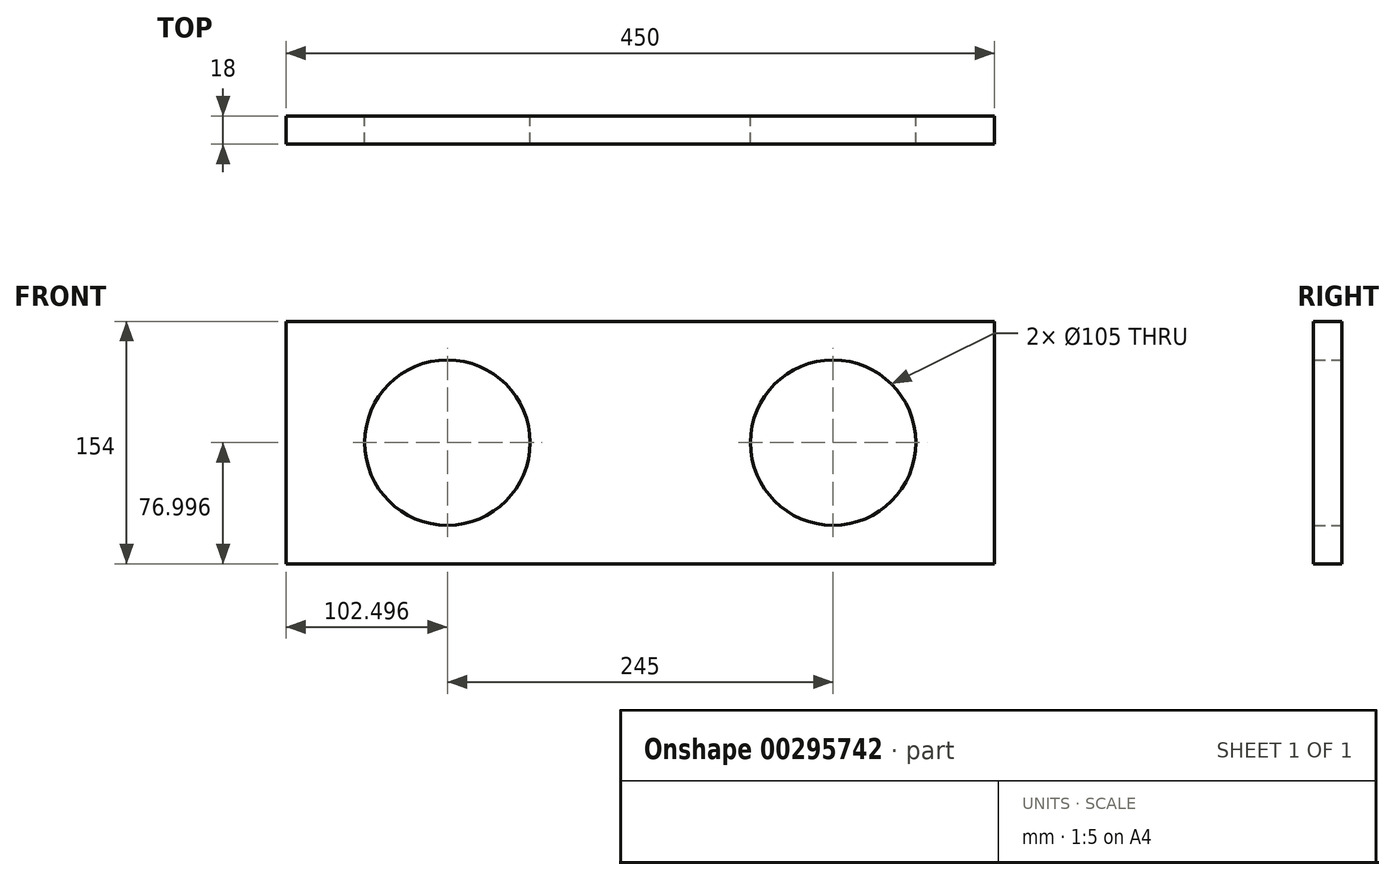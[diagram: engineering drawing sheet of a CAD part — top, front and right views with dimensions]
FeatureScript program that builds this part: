
annotation { "Feature Type Name" : "Feature", "Feature Type Description" : "" }
export const myFeature = defineFeature(function(context is Context, id is Id, definition is map)
    precondition{}
    {
        {
            var Q0;
            Q0=qCreatedBy(makeId("Front.planeOp"),FACE);
            var sketch = newSketch(context, id + "F0", { "sketchPlane" : qUnion([Q0])});
            skLineSegment(sketch, "E0.bottom", {"start": v(-254.75, 80.19) * mm, "end": v(195.25, 80.19) * mm});
            skLineSegment(sketch, "E0.top", {"start": v(-254.75, -73.81) * mm, "end": v(195.25, -73.81) * mm});
            skLineSegment(sketch, "E0.left", {"start": v(-254.75, 80.19) * mm, "end": v(-254.75, -73.81) * mm});
            skLineSegment(sketch, "E0.right", {"start": v(195.25, 80.19) * mm, "end": v(195.25, -73.81) * mm});
            skLineSegment(sketch, "E1", {"start": v(-254.75, 3.19) * mm, "end": v(195.25, 3.19) * mm, "construction": true});
            skCircle(sketch, "E2", {"center": v(-152.25, 3.19) * mm, "radius": 52.5 * mm});
            skCircle(sketch, "E3", {"center": v(92.75, 3.19) * mm, "radius": 52.5 * mm});
            skSolve(sketch);
        }
        {
            var Q0;
            Q0=makeQuery(id+"F0.imprint","IMPRINT",FACE,{"disambiguationData":[TD([[makeQuery(id+"F0.imprint","IMPRINT",EDGE,{"derivedFrom":sQuery(id+"F0.wireOp",EDGE,"E0.bottom")}),-1.0]])]});
            extrude(context, id + "F1", {"entities" : qUnion([Q0]), "depth" : 18 * mm});
        }
    });
